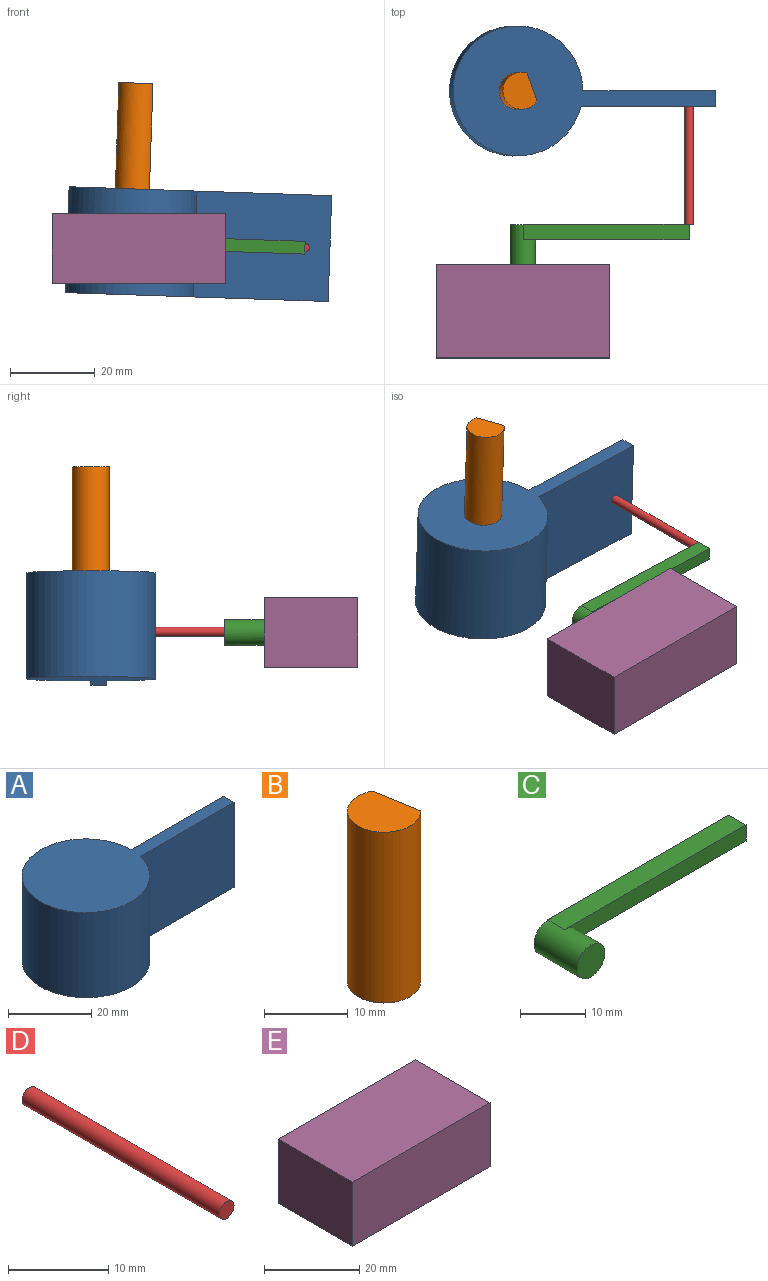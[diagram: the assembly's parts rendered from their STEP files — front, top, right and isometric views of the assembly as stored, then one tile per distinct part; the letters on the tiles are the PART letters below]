
ASSEMBLY  parts=5 mates=4
PART A: 6 faces, bbox 62.1x30.7x25 mm
  f0: cylinder r=15.33mm len=30.67mm, axis (0,0,-1), area 2318.5mm2, adj f1,f3,f4,f5
  f1: plane 31.81x25mm, normal (0,-1,0), area 795.2mm2, adj f0,f2,f4,f5
  f2: plane 25x3.57mm, normal (1,0,0), area 89.1mm2, adj f1,f3,f4,f5
  f3: plane 31.39x25mm, normal (0,1,0), area 784.7mm2, adj f0,f2,f4,f5
  f4: plane 62.06x30.67mm, normal (0,0,1), area 851mm2, adj f0,f1,f2,f3
  f5: plane 62.06x30.67mm, normal (0,0,-1), area 851mm2, adj f0,f1,f2,f3
PART B: 4 faces, bbox 7.5x8.8x25 mm
  f0: plane 25x6.97mm, normal (0.99,0.16,0), area 176.6mm2, adj f1,f2,f3
  f1: cylinder r=4.39mm len=25mm, axis (0,0,-1), area 483.6mm2, adj f0,f2,f3
  f2: plane 8.77x7.53mm, normal (0,0,1), area 51.6mm2, adj f0,f1
  f3: plane 8.77x7.53mm, normal (0,0,-1), area 51.6mm2, adj f0,f1
PART C: 9 faces, bbox 42.2x9.4x6 mm
  f0: cylinder r=3mm len=9.3mm, axis (0,-1,0), area 158.4mm2, adj f1,f2,f4,f5,f8
  f1: plane 6x6mm, normal (0,1,0), area 28.3mm2, adj f0,f3
  f2: plane 6x6mm, normal (0,-1,0), area 28.3mm2, adj f0
  f3: cylinder r=3mm len=3mm, axis (0,-1,0), area 0.5mm2, adj f1,f4,f5,f7
  f4: plane 36.19x3.7mm, normal (0,0,-1), area 133.9mm2, adj f0,f3,f6,f7,f8
  f5: plane 39.19x3.7mm, normal (0,0,1), area 145mm2, adj f0,f3,f6,f7,f8
  f6: plane 3.7x3mm, normal (1,0,0), area 11.1mm2, adj f4,f5,f7,f8
  f7: plane 39.19x3mm, normal (0,1,0), area 110.5mm2, adj f3,f4,f5,f6
  f8: plane 39.19x3mm, normal (0,-1,0), area 110.5mm2, adj f0,f4,f5,f6
PART D: 3 faces, bbox 2.1x27.9x2.1 mm
  f0: cylinder r=1.04mm len=27.9mm, axis (0,-1,0), area 182mm2, adj f1,f2
  f1: plane 2.08x2.08mm, normal (0,1,0), area 3.4mm2, adj f0
  f2: plane 2.08x2.08mm, normal (0,-1,0), area 3.4mm2, adj f0
PART E: 6 faces, bbox 40.9x22.2x16.5 mm
  f0: plane 40.86x16.5mm, normal (0,1,0), area 674.1mm2, adj f1,f3,f4,f5
  f1: plane 22.16x16.5mm, normal (-1,0,0), area 365.6mm2, adj f0,f2,f4,f5
  f2: plane 40.86x16.5mm, normal (0,-1,0), area 674.1mm2, adj f1,f3,f4,f5
  f3: plane 22.16x16.5mm, normal (1,0,0), area 365.6mm2, adj f0,f2,f4,f5
  f4: plane 40.86x22.16mm, normal (0,0,1), area 905.3mm2, adj f0,f1,f2,f3
  f5: plane 40.86x22.16mm, normal (0,0,-1), area 905.3mm2, adj f0,f1,f2,f3
PLACE A rot(axis=(0,1,0),1.9deg) t=(-28.14,0.62,0.04)mm
PLACE B rot(axis=(0.02,0.18,0.98),10.8deg) t=(-28.14,0.62,0.04)mm
PLACE C rot(axis=(0,1,0),1.9deg) t=(-40.01,-4.37,4.14)mm
PLACE D rot(axis=(0,1,0),1.9deg) t=(-32.42,-4.37,3.84)mm
PLACE E t=(-41.9,-4.37,2.73)mm fixed
MATE fastened D.f0 <-> C.f7  axis (0,-1,0) through (13.07,-30.84,11.16)mm
MATE revolute C.f0 <-> E.f0  axis (0,-1,0) through (-26.14,-40.24,10.98)mm
MATE revolute B.f1 <-> A.f0  axis (-0.03,0,-1) through (-27.3,0.62,25.03)mm
MATE fastened D.f0 <-> A.f1  axis (0,1,0) through (13.07,-2.94,11.16)mm
